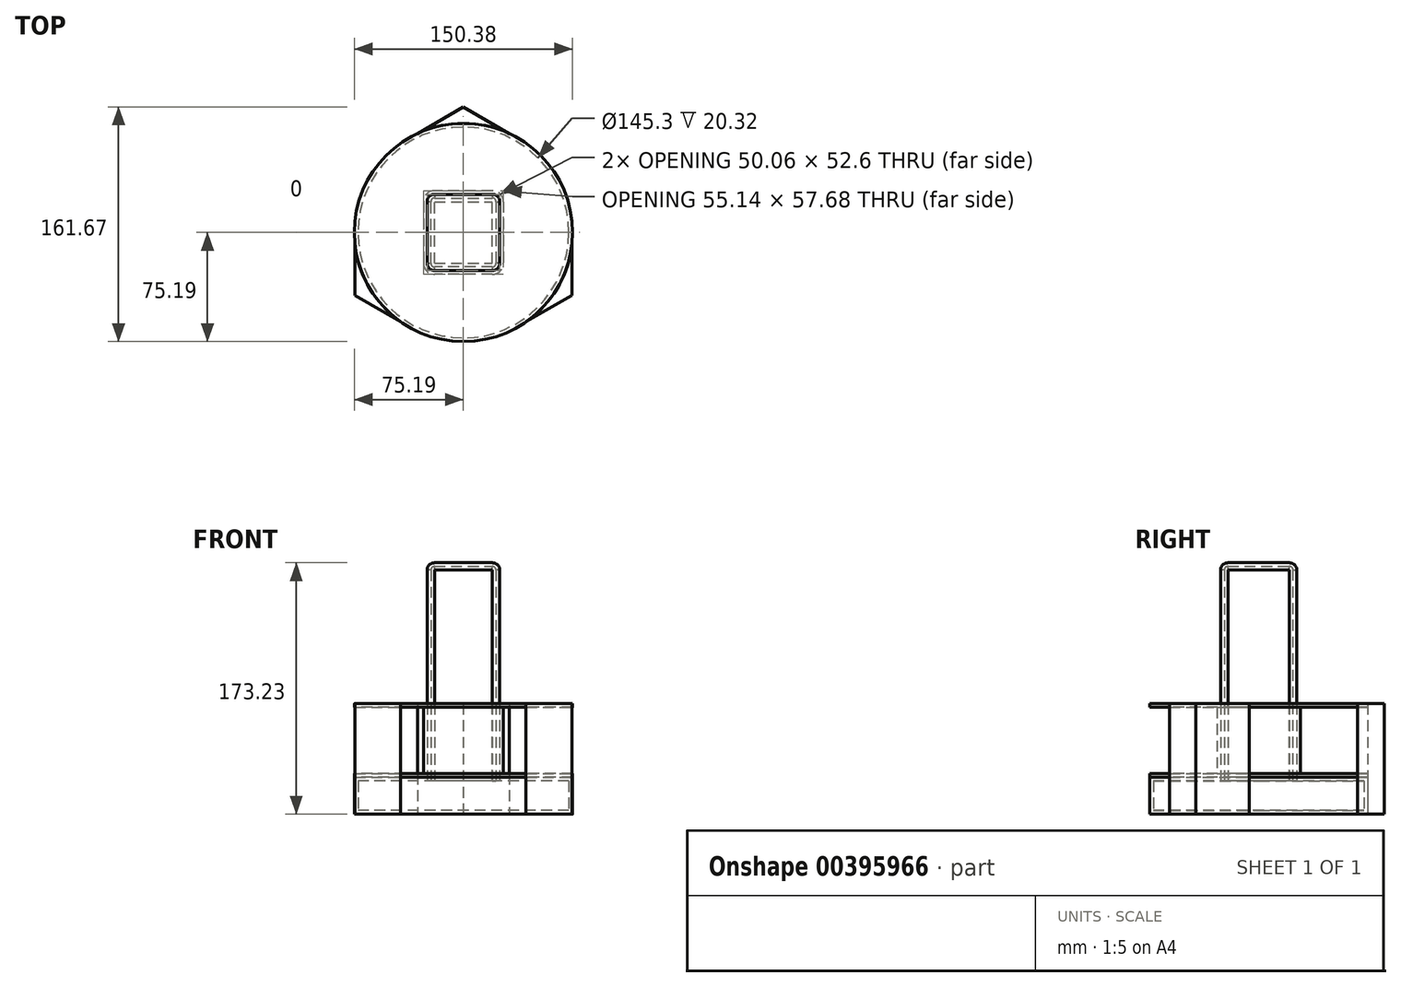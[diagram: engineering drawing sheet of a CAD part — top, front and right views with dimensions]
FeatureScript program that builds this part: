
annotation { "Feature Type Name" : "Feature", "Feature Type Description" : "" }
export const myFeature = defineFeature(function(context is Context, id is Id, definition is map)
    precondition{}
    {
        {
            var Q0;
            Q0=qCreatedBy(makeId("Top.planeOp"),FACE);
            var sketch = newSketch(context, id + "F0", { "sketchPlane" : qUnion([Q0])});
            skCircle(sketch, "E0", {"center": v(0, 0) * mm, "radius": 75.2 * mm});
            skSolve(sketch);
        }
        {
            var Q0;
            Q0=makeQuery(id+"F0.imprint","IMPRINT",FACE,{"disambiguationData":[TD([[makeQuery(id+"F0.imprint","IMPRINT",EDGE,{"derivedFrom":sQuery(id+"F0.wireOp",EDGE,"E0")}),1.0]])]});
            var sketch = newSketch(context, id + "F1", { "sketchPlane" : qUnion([Q0])});
            skCircle(sketch, "E1.cCircle", {"center": v(0, 0) * mm, "radius": 74.9 * mm, "construction": true});
            skLineSegment(sketch, "E1.0", {"start": v(-74.9, -43.24) * mm, "end": v(-74.9, 43.24) * mm});
            skLineSegment(sketch, "E1.1", {"start": v(-74.9, 43.24) * mm, "end": v(0, 86.48) * mm});
            skLineSegment(sketch, "E1.2", {"start": v(0, 86.48) * mm, "end": v(74.9, 43.24) * mm});
            skLineSegment(sketch, "E1.3", {"start": v(74.9, 43.24) * mm, "end": v(74.9, -43.24) * mm});
            skLineSegment(sketch, "E1.4", {"start": v(74.9, -43.24) * mm, "end": v(0, -86.48) * mm});
            skLineSegment(sketch, "E1.5", {"start": v(0, -86.48) * mm, "end": v(-74.9, -43.24) * mm});
            skPoint(sketch, "E1.0.midPoint", {"position": v(-74.9, 0) * mm});
            skSolve(sketch);
        }
        {
            var Q0;
            {var subQ0=sQuery(id+"F1.wireOp",EDGE,"E1.5");var subQ1=sQuery(id+"F1.wireOp",EDGE,"E1.0");var subQ2=makeQuery(id+"F1.imprint","INTERSECT",VERTEX,{"derivedFrom":[subQ1,subQ0]});Q0=makeQuery(id+"F1.imprint","IMPRINT",FACE,{"disambiguationData":[TD([[makeQuery(id+"F1.imprint","IMPRINT",EDGE,{"disambiguationData":[TD([[subQ2,-1.0]])],"derivedFrom":subQ1}),-1.0]])]});}
            var Q1;
            {var subQ0=sQuery(id+"F1.wireOp",EDGE,"E1.2");var subQ1=sQuery(id+"F1.wireOp",EDGE,"E1.1");var subQ2=makeQuery(id+"F1.imprint","INTERSECT",VERTEX,{"derivedFrom":[subQ1,subQ0]});Q1=makeQuery(id+"F1.imprint","IMPRINT",FACE,{"disambiguationData":[TD([[makeQuery(id+"F1.imprint","IMPRINT",EDGE,{"disambiguationData":[TD([[subQ2,1.0]])],"derivedFrom":subQ1}),-1.0]])]});}
            var Q2;
            {var subQ0=sQuery(id+"F1.wireOp",EDGE,"E1.4");var subQ1=sQuery(id+"F1.wireOp",EDGE,"E1.3");var subQ2=makeQuery(id+"F1.imprint","INTERSECT",VERTEX,{"derivedFrom":[subQ1,subQ0]});Q2=makeQuery(id+"F1.imprint","IMPRINT",FACE,{"disambiguationData":[TD([[makeQuery(id+"F1.imprint","IMPRINT",EDGE,{"disambiguationData":[TD([[subQ2,1.0]])],"derivedFrom":subQ1}),-1.0]])]});}
            extrude(context, id + "F2", {"entities" : qUnion([Q0, Q1, Q2]), "depth" : 76.2 * mm});
        }
        {
            var Q0;
            Q0=makeQuery(id+"F0.imprint","IMPRINT",FACE,{"disambiguationData":[TD([[makeQuery(id+"F0.imprint","IMPRINT",EDGE,{"derivedFrom":sQuery(id+"F0.wireOp",EDGE,"E0")}),1.0]])]});
            extrude(context, id + "F3", {"entities" : qUnion([Q0]), "depth" : 25.4 * mm});
        }
        {
            var Q0;
            Q0=makeQuery(id+"F3.opExtrude","CAP_FACE",FACE,{"disambiguationData":[OSD([sQuery(id+"F0.wireOp",EDGE,"E0")])],"isStart":false});
            var sketch = newSketch(context, id + "F4", { "sketchPlane" : qUnion([Q0])});
            skLineSegment(sketch, "E2.bottom", {"start": v(25.03, 26.3) * mm, "end": v(-25.03, 26.3) * mm});
            skLineSegment(sketch, "E2.top", {"start": v(25.03, -26.3) * mm, "end": v(-25.03, -26.3) * mm});
            skLineSegment(sketch, "E2.left", {"start": v(25.03, 26.3) * mm, "end": v(25.03, -26.3) * mm});
            skLineSegment(sketch, "E2.right", {"start": v(-25.03, 26.3) * mm, "end": v(-25.03, -26.3) * mm});
            skPoint(sketch, "E2.middle", {"position": v(0, 0) * mm});
            skSolve(sketch);
        }
        {
            var Q0;
            Q0=makeQuery(id+"F4.imprint","IMPRINT",FACE,{"disambiguationData":[TD([[makeQuery(id+"F4.imprint","IMPRINT",EDGE,{"derivedFrom":sQuery(id+"F4.wireOp",EDGE,"E2.bottom")}),1.0]])]});
            extrude(context, id + "F5", {"entities" : qUnion([Q0]), "operationType" : NewBodyOperationType.ADD, "depth" : 147.83 * mm});
        }
        {
            var Q0;
            Q0=makeQuery(id+"F5.opExtrude","SWEPT_EDGE",EDGE,{"disambiguationData":[OSD([sQuery(id+"F4.wireOp",EDGE,"E2.top"),sQuery(id+"F4.wireOp",EDGE,"E2.left")])]});
            var Q1;
            Q1=makeQuery(id+"F5.opExtrude","SWEPT_EDGE",EDGE,{"disambiguationData":[OSD([sQuery(id+"F4.wireOp",EDGE,"E2.bottom"),sQuery(id+"F4.wireOp",EDGE,"E2.left")])]});
            var Q2;
            Q2=makeQuery(id+"F5.opExtrude","SWEPT_EDGE",EDGE,{"disambiguationData":[OSD([sQuery(id+"F4.wireOp",EDGE,"E2.bottom"),sQuery(id+"F4.wireOp",EDGE,"E2.right")])]});
            var Q3;
            Q3=makeQuery(id+"F5.opExtrude","SWEPT_EDGE",EDGE,{"disambiguationData":[OSD([sQuery(id+"F4.wireOp",EDGE,"E2.top"),sQuery(id+"F4.wireOp",EDGE,"E2.right")])]});
            var Q4;
            Q4=makeQuery(id+"F5.opExtrude","CAP_EDGE",EDGE,{"disambiguationData":[OSD([sQuery(id+"F4.wireOp",EDGE,"E2.right")])],"isStart":false});
            var Q5;
            Q5=makeQuery(id+"F5.opExtrude","CAP_EDGE",EDGE,{"disambiguationData":[OSD([sQuery(id+"F4.wireOp",EDGE,"E2.top")])],"isStart":false});
            var Q6;
            Q6=makeQuery(id+"F5.opExtrude","CAP_EDGE",EDGE,{"disambiguationData":[OSD([sQuery(id+"F4.wireOp",EDGE,"E2.bottom")])],"isStart":false});
            var Q7;
            Q7=makeQuery(id+"F5.opExtrude","CAP_EDGE",EDGE,{"disambiguationData":[OSD([sQuery(id+"F4.wireOp",EDGE,"E2.left")])],"isStart":false});
            fillet(context, id + "F6", {"entities" : qUnion([Q0, Q1, Q2, Q3, Q4, Q5, Q6, Q7]), "radius" : 5.08 * mm, "tangentPropagation" : true, "allowEdgeOverflow" : false});
        }
        {
            var Q0;
            Q0=makeQuery(id+"F3.opExtrude","CAP_FACE",FACE,{"disambiguationData":[OSD([sQuery(id+"F0.wireOp",EDGE,"E0")])],"isStart":false});
            extrude(context, id + "F7", {"entities" : qUnion([Q0]), "depth" : 50.8 * mm});
        }
        {
            var Q0;
            Q0=makeQuery(id+"F7.opExtrude","SWEPT_FACE",FACE,{"disambiguationData":[OSD([sQuery(id+"F0.wireOp",EDGE,"E0")])]});
            shell(context, id + "F8", {"entities" : qUnion([Q0]), "thickness" : 2.54 * mm});
        }
        {
            var Q0;
            Q0=makeQuery(id+"F5.opExtrude","SWEPT_FACE",FACE,{"disambiguationData":[OSD([sQuery(id+"F4.wireOp",EDGE,"E2.right")])]});
            var Q1;
            Q1=makeQuery(id+"F5.opExtrude","SWEPT_FACE",FACE,{"disambiguationData":[OSD([sQuery(id+"F4.wireOp",EDGE,"E2.bottom")])]});
            var Q2;
            Q2=makeQuery(id+"F5.opExtrude","SWEPT_FACE",FACE,{"disambiguationData":[OSD([sQuery(id+"F4.wireOp",EDGE,"E2.left")])]});
            var Q3;
            Q3=makeQuery(id+"F5.opExtrude","SWEPT_FACE",FACE,{"disambiguationData":[OSD([sQuery(id+"F4.wireOp",EDGE,"E2.top")])]});
            shell(context, id + "F9", {"entities" : qUnion([Q0, Q1, Q2, Q3]), "thickness" : 2.54 * mm});
        }
        {
            var Q0;
            Q0=makeQuery(id+"F5.opExtrude","CAP_FACE",FACE,{"disambiguationData":[OSD([sQuery(id+"F4.wireOp",EDGE,"E2.bottom"),sQuery(id+"F4.wireOp",EDGE,"E2.top"),sQuery(id+"F4.wireOp",EDGE,"E2.left"),sQuery(id+"F4.wireOp",EDGE,"E2.right")])],"isStart":false});
            extrude(context, id + "F10", {"entities" : qUnion([Q0]), "operationType" : NewBodyOperationType.ADD, "oppositeDirection" : true, "depth" : 99.82 * mm});
        }
    });
